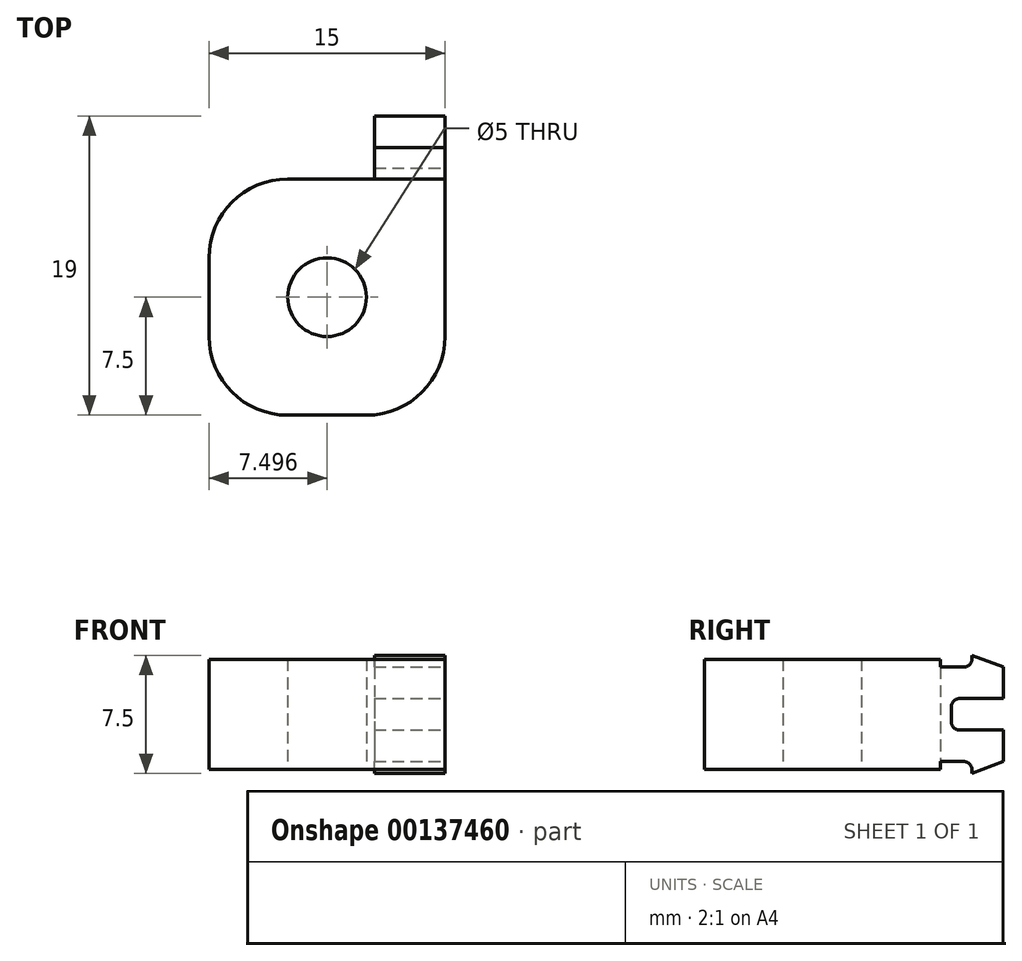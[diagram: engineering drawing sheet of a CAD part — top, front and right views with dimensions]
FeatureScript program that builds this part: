
annotation { "Feature Type Name" : "Feature", "Feature Type Description" : "" }
export const myFeature = defineFeature(function(context is Context, id is Id, definition is map)
    precondition{}
    {
        {
            var Q0;
            Q0=qCreatedBy(makeId("Top.planeOp"),FACE);
            var sketch = newSketch(context, id + "F0", { "sketchPlane" : qUnion([Q0])});
            skLineSegment(sketch, "E0.bottom", {"start": v(-17.42, 0) * mm, "end": v(-2.42, 0) * mm});
            skLineSegment(sketch, "E0.top", {"start": v(-17.42, 35) * mm, "end": v(-2.42, 35) * mm});
            skLineSegment(sketch, "E0.left", {"start": v(-17.42, 0) * mm, "end": v(-17.42, 35) * mm});
            skLineSegment(sketch, "E0.right", {"start": v(-2.42, 0) * mm, "end": v(-2.42, 35) * mm});
            skLineSegment(sketch, "E1", {"start": v(-17.42, 15) * mm, "end": v(-2.42, 15) * mm});
            skCircle(sketch, "E2", {"center": v(-9.92, 7.5) * mm, "radius": 2.5 * mm});
            skPoint(sketch, "E3", {"position": v(-9.92, 35) * mm});
            skLineSegment(sketch, "E4.bottom", {"start": v(-17.42, 22.95) * mm, "end": v(-16.17, 22.95) * mm});
            skLineSegment(sketch, "E4.top", {"start": v(-17.42, 17.05) * mm, "end": v(-16.17, 17.05) * mm});
            skLineSegment(sketch, "E4.left", {"start": v(-17.42, 22.95) * mm, "end": v(-17.42, 17.05) * mm});
            skLineSegment(sketch, "E4.right", {"start": v(-16.17, 22.95) * mm, "end": v(-16.17, 17.05) * mm});
            skLineSegment(sketch, "E5.bottom", {"start": v(-2.42, 22.95) * mm, "end": v(-3.67, 22.95) * mm});
            skLineSegment(sketch, "E5.top", {"start": v(-2.42, 17.05) * mm, "end": v(-3.67, 17.05) * mm});
            skLineSegment(sketch, "E5.left", {"start": v(-2.42, 22.95) * mm, "end": v(-2.42, 17.05) * mm});
            skLineSegment(sketch, "E5.right", {"start": v(-3.67, 22.95) * mm, "end": v(-3.67, 17.05) * mm});
            skPoint(sketch, "E6", {"position": v(-16.17, 20) * mm});
            skCircle(sketch, "E7", {"center": v(-9.92, 20) * mm, "radius": 2.3 * mm});
            skSolve(sketch);
        }
        {
            var Q0;
            {var subQ2=sQuery(id+"F0.wireOp",EDGE,"E0.bottom");Q0=makeQuery(id+"F0.imprint","IMPRINT",FACE,{"disambiguationData":[TD([[makeQuery(id+"F0.imprint","IMPRINT",EDGE,{"derivedFrom":subQ2}),1.0]])]});}
            extrude(context, id + "F1", {"entities" : qUnion([Q0]), "depth" : 7 * mm});
        }
        {
            var Q0;
            Q0=makeQuery(id+"F1.opExtrude","SWEPT_FACE",FACE,{"disambiguationData":[OSD([sQuery(id+"F0.wireOp",EDGE,"E0.right")])]});
            var sketch = newSketch(context, id + "F2", { "sketchPlane" : qUnion([Q0])});
            skLineSegment(sketch, "E8.bottom", {"start": v(15, 6.5) * mm, "end": v(19, 6.5) * mm});
            skLineSegment(sketch, "E8.top", {"start": v(15, 4.5) * mm, "end": v(19, 4.5) * mm});
            skLineSegment(sketch, "E8.left", {"start": v(15, 6.5) * mm, "end": v(15, 4.5) * mm});
            skLineSegment(sketch, "E8.right", {"start": v(19, 6.5) * mm, "end": v(19, 4.5) * mm});
            skLineSegment(sketch, "E9.bottom", {"start": v(15, 2.5) * mm, "end": v(19, 2.5) * mm});
            skLineSegment(sketch, "E9.top", {"start": v(15, 0.5) * mm, "end": v(19, 0.5) * mm});
            skLineSegment(sketch, "E9.left", {"start": v(15, 2.5) * mm, "end": v(15, 0.5) * mm});
            skLineSegment(sketch, "E9.right", {"start": v(19, 2.5) * mm, "end": v(19, 0.5) * mm});
            skLineSegment(sketch, "E10", {"start": v(19, 4.5) * mm, "end": v(19, 2.5) * mm});
            skPoint(sketch, "E11", {"position": v(19, 3.5) * mm});
            skPoint(sketch, "E12", {"position": v(0, 3.5) * mm});
            skLineSegment(sketch, "E13", {"start": v(17, 6.5) * mm, "end": v(17, 7.25) * mm});
            skLineSegment(sketch, "E14", {"start": v(17, 0.5) * mm, "end": v(17, -0.25) * mm});
            skLineSegment(sketch, "E15", {"start": v(17, -0.25) * mm, "end": v(19, 0.5) * mm});
            skLineSegment(sketch, "E16", {"start": v(17, 7.25) * mm, "end": v(19, 6.5) * mm});
            skLineSegment(sketch, "E17", {"start": v(15.7, 4.5) * mm, "end": v(15.7, 2.5) * mm});
            skSolve(sketch);
        }
        {
            var Q0;
            {var subQ2=sQuery(id+"F2.wireOp",EDGE,"E13");Q0=makeQuery(id+"F2.imprint","IMPRINT",FACE,{"disambiguationData":[TD([[makeQuery(id+"F2.imprint","IMPRINT",EDGE,{"derivedFrom":subQ2}),-1.0]])]});}
            var Q1;
            {var subQ3=sQuery(id+"F2.wireOp",EDGE,"E8.left");Q1=makeQuery(id+"F2.imprint","IMPRINT",FACE,{"disambiguationData":[TD([[makeQuery(id+"F2.imprint","IMPRINT",EDGE,{"derivedFrom":subQ3}),1.0]])]});}
            var Q2;
            {var subQ3=sQuery(id+"F2.wireOp",EDGE,"E17");Q2=makeQuery(id+"F2.imprint","IMPRINT",FACE,{"disambiguationData":[TD([[makeQuery(id+"F2.imprint","IMPRINT",EDGE,{"derivedFrom":subQ3}),-1.0]])]});}
            var Q3;
            {var subQ3=sQuery(id+"F2.wireOp",EDGE,"E9.left");Q3=makeQuery(id+"F2.imprint","IMPRINT",FACE,{"disambiguationData":[TD([[makeQuery(id+"F2.imprint","IMPRINT",EDGE,{"derivedFrom":subQ3}),1.0]])]});}
            var Q4;
            {var subQ2=sQuery(id+"F2.wireOp",EDGE,"E14");Q4=makeQuery(id+"F2.imprint","IMPRINT",FACE,{"disambiguationData":[TD([[makeQuery(id+"F2.imprint","IMPRINT",EDGE,{"derivedFrom":subQ2}),1.0]])]});}
            extrude(context, id + "F3", {"entities" : qUnion([Q0, Q1, Q2, Q3, Q4]), "operationType" : NewBodyOperationType.ADD, "oppositeDirection" : true, "depth" : 4.5 * mm});
        }
        {
            var Q0;
            Q0=makeQuery(id+"F3.opExtrude","SWEPT_EDGE",EDGE,{"disambiguationData":[OSD([sQuery(id+"F0.wireOp",EDGE,"E0.right"),sQuery(id+"F0.wireOp",EDGE,"E1"),sQuery(id+"F2.wireOp",EDGE,"E9.top"),sQuery(id+"F2.wireOp",EDGE,"E9.left")])]});
            var Q1;
            Q1=makeQuery(id+"F3.opExtrude","SWEPT_EDGE",EDGE,{"disambiguationData":[OSD([sQuery(id+"F0.wireOp",EDGE,"E0.right"),sQuery(id+"F0.wireOp",EDGE,"E1"),sQuery(id+"F2.wireOp",EDGE,"E8.bottom"),sQuery(id+"F2.wireOp",EDGE,"E8.left")])]});
            var Q2;
            Q2=makeQuery(id+"F3.opExtrude","SWEPT_EDGE",EDGE,{"disambiguationData":[OSD([sQuery(id+"F2.wireOp",EDGE,"E9.bottom"),sQuery(id+"F2.wireOp",EDGE,"E17")])]});
            var Q3;
            Q3=makeQuery(id+"F3.opExtrude","SWEPT_EDGE",EDGE,{"disambiguationData":[OSD([sQuery(id+"F2.wireOp",EDGE,"E8.top"),sQuery(id+"F2.wireOp",EDGE,"E17")])]});
            var Q4;
            Q4=makeQuery(id+"F3.opExtrude","SWEPT_EDGE",EDGE,{"disambiguationData":[OSD([sQuery(id+"F2.wireOp",EDGE,"E9.top"),sQuery(id+"F2.wireOp",EDGE,"E14")])]});
            var Q5;
            Q5=makeQuery(id+"F3.opExtrude","SWEPT_EDGE",EDGE,{"disambiguationData":[OSD([sQuery(id+"F2.wireOp",EDGE,"E8.bottom"),sQuery(id+"F2.wireOp",EDGE,"E13")])]});
            fillet(context, id + "F4", {"entities" : qUnion([Q0, Q1, Q2, Q3, Q4, Q5]), "radius" : 0.5 * mm, "tangentPropagation" : true, "allowEdgeOverflow" : false});
        }
        {
            var Q0;
            Q0=makeQuery(id+"F1.opExtrude","SWEPT_EDGE",EDGE,{"disambiguationData":[OSD([sQuery(id+"F0.wireOp",EDGE,"E0.left"),sQuery(id+"F0.wireOp",EDGE,"E1")])]});
            var Q1;
            Q1=makeQuery(id+"F1.opExtrude","SWEPT_EDGE",EDGE,{"disambiguationData":[OSD([sQuery(id+"F0.wireOp",EDGE,"E0.bottom"),sQuery(id+"F0.wireOp",EDGE,"E0.left")])]});
            var Q2;
            Q2=makeQuery(id+"F1.opExtrude","SWEPT_EDGE",EDGE,{"disambiguationData":[OSD([sQuery(id+"F0.wireOp",EDGE,"E0.bottom"),sQuery(id+"F0.wireOp",EDGE,"E0.right")])]});
            fillet(context, id + "F5", {"entities" : qUnion([Q0, Q1, Q2]), "radius" : 5 * mm, "tangentPropagation" : true, "allowEdgeOverflow" : false});
        }
    });
